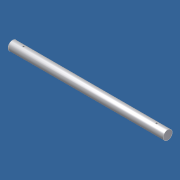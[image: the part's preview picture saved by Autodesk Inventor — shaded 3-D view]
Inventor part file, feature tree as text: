
AUTODESK INVENTOR PART (.ipt)
format: ipt  version: unknown  size: 173,056 bytes
history: native  units: in
note: dims shown in document units (in); Inventor stores cm internally (conversion verified against a paired STEP export)
features: sketch x2, revolve x1, plane x1, hole x1
ambient origin geometry x8: Origin, YZ Plane, XZ Plane, XY Plane, X Axis, Y Axis, Z Axis, Center Point
bodies: Solid1 (feature_tree)
feature tree (5):
  revolve  "Revolution1"  [1 undecoded]
  plane  "Work Plane1"
  hole  "Hole1"  [1 undecoded]
  sketch  "Sketch1"  dims[d0=5.25in d1=0.1557in]
  sketch  "Sketch2"  dims[d2=90.0deg d3=0.375in d4=0.375in d5=0.06in d6=0.75in d7=0.375in d8=0.25in d9=0.5635in d10=1.0in d11=0.0in]
note: 2 required parameter values undecoded (feature->parameter linkage not recoverable at this tier; creation-order binding heuristic only, values carry confidence <= 0.55)